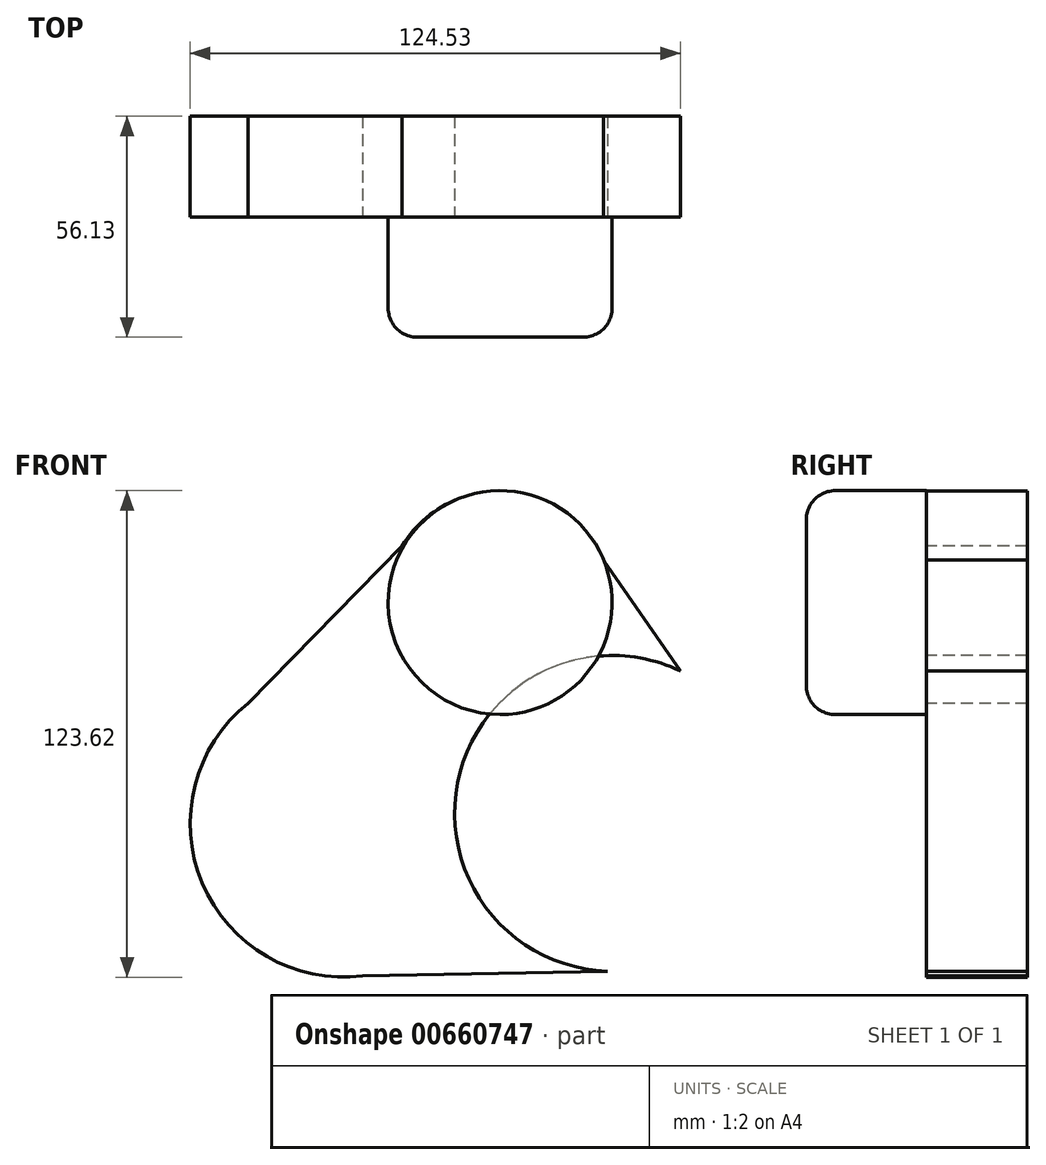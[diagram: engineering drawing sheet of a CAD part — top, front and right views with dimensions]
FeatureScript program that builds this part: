
annotation { "Feature Type Name" : "Feature", "Feature Type Description" : "" }
export const myFeature = defineFeature(function(context is Context, id is Id, definition is map)
    precondition{}
    {
        {
            var Q0;
            Q0=qCreatedBy(makeId("Front.planeOp"),FACE);
            var sketch = newSketch(context, id + "F0", { "sketchPlane" : qUnion([Q0])});
            skCircle(sketch, "E0", {"center": v(-18.53, 30.7) * mm, "radius": 28.78 * mm});
            skCircle(sketch, "E1", {"center": v(-57.98, -24.98) * mm, "radius": 39.05 * mm});
            skCircle(sketch, "E2", {"center": v(10.23, -22.4) * mm, "radius": 40.1 * mm});
            skLineSegment(sketch, "E3", {"start": v(-82.28, 5.58) * mm, "end": v(-43.17, 45.57) * mm});
            skLineSegment(sketch, "E4", {"start": v(7.96, 41.95) * mm, "end": v(27.5, 13.8) * mm});
            skLineSegment(sketch, "E5", {"start": v(-53.18, -63.73) * mm, "end": v(8.94, -62.48) * mm});
            skSolve(sketch);
        }
        {
            var Q0;
            {var subQ0=sQuery(id+"F0.wireOp",EDGE,"E2");var subQ1=sQuery(id+"F0.wireOp",EDGE,"E0");var subQ2=makeQuery(id+"F0.imprint","INTERSECT",VERTEX,{"disambiguationData":[OD(0.0)],"derivedFrom":[subQ1,subQ0]});Q0=makeQuery(id+"F0.imprint","IMPRINT",FACE,{"disambiguationData":[TD([[makeQuery(id+"F0.imprint","IMPRINT",EDGE,{"disambiguationData":[TD([[subQ2,-1.0]])],"derivedFrom":subQ1}),1.0]])]});}
            var Q1;
            {var subQ0=sQuery(id+"F0.wireOp",EDGE,"E4");Q1=makeQuery(id+"F0.imprint","IMPRINT",FACE,{"disambiguationData":[TD([[makeQuery(id+"F0.imprint","IMPRINT",EDGE,{"derivedFrom":subQ0}),-1.0]])]});}
            var Q2;
            {var subQ0=sQuery(id+"F0.wireOp",EDGE,"E5");Q2=makeQuery(id+"F0.imprint","IMPRINT",FACE,{"disambiguationData":[TD([[makeQuery(id+"F0.imprint","IMPRINT",EDGE,{"derivedFrom":subQ0}),1.0]])]});}
            var Q3;
            {var subQ0=sQuery(id+"F0.wireOp",EDGE,"E2");var subQ1=sQuery(id+"F0.wireOp",EDGE,"E1");var subQ2=makeQuery(id+"F0.imprint","INTERSECT",VERTEX,{"disambiguationData":[OD(0.0)],"derivedFrom":[subQ1,subQ0]});Q3=makeQuery(id+"F0.imprint","IMPRINT",FACE,{"disambiguationData":[TD([[makeQuery(id+"F0.imprint","IMPRINT",EDGE,{"disambiguationData":[TD([[subQ2,1.0]])],"derivedFrom":subQ1}),1.0]])]});}
            var Q4;
            {var subQ0=sQuery(id+"F0.wireOp",EDGE,"E2");var subQ1=sQuery(id+"F0.wireOp",EDGE,"E0");var subQ2=makeQuery(id+"F0.imprint","INTERSECT",VERTEX,{"disambiguationData":[OD(0.0)],"derivedFrom":[subQ1,subQ0]});Q4=makeQuery(id+"F0.imprint","IMPRINT",FACE,{"disambiguationData":[TD([[makeQuery(id+"F0.imprint","IMPRINT",EDGE,{"disambiguationData":[TD([[subQ2,-1.0]])],"derivedFrom":subQ1}),-1.0]])]});}
            var Q5;
            {var subQ0=sQuery(id+"F0.wireOp",EDGE,"E0");var subQ1=makeQuery(id+"F0.imprint","INTERSECT",VERTEX,{"derivedFrom":[subQ0,sQuery(id+"F0.wireOp",EDGE,"E3")]});Q5=makeQuery(id+"F0.imprint","IMPRINT",FACE,{"disambiguationData":[TD([[makeQuery(id+"F0.imprint","IMPRINT",EDGE,{"disambiguationData":[TD([[subQ1,1.0]])],"derivedFrom":subQ0}),1.0]])]});}
            var Q6;
            {var subQ0=sQuery(id+"F0.wireOp",EDGE,"E3");Q6=makeQuery(id+"F0.imprint","IMPRINT",FACE,{"disambiguationData":[TD([[makeQuery(id+"F0.imprint","IMPRINT",EDGE,{"derivedFrom":subQ0}),-1.0]])]});}
            var Q7;
            {var subQ0=sQuery(id+"F0.wireOp",EDGE,"E1");var subQ1=makeQuery(id+"F0.imprint","INTERSECT",VERTEX,{"derivedFrom":[subQ0,sQuery(id+"F0.wireOp",EDGE,"E3")]});Q7=makeQuery(id+"F0.imprint","IMPRINT",FACE,{"disambiguationData":[TD([[makeQuery(id+"F0.imprint","IMPRINT",EDGE,{"disambiguationData":[TD([[subQ1,1.0]])],"derivedFrom":subQ0}),1.0]])]});}
            extrude(context, id + "F1", {"entities" : qUnion([Q0, Q1, Q2, Q3, Q4, Q5, Q6, Q7]), "oppositeDirection" : true, "depth" : 25.65 * mm, "offsetDistance" : 25.4 * mm});
        }
        {
            var Q0;
            Q0=qCreatedBy(makeId("Front.planeOp"),FACE);
            var sketch = newSketch(context, id + "F2", { "sketchPlane" : qUnion([Q0])});
            skCircle(sketch, "E6", {"center": v(-18.3, 31.15) * mm, "radius": 28.44 * mm});
            skSolve(sketch);
        }
        {
            var Q0;
            Q0 = qSketchRegion(id + "F2", true);
            extrude(context, id + "F3", {"entities" : qUnion([Q0]), "operationType" : NewBodyOperationType.ADD, "depth" : 30.48 * mm, "offsetDistance" : 25.4 * mm});
        }
        {
            var Q0;
            Q0=makeQuery(id+"F3.opExtrude","CAP_EDGE",EDGE,{"disambiguationData":[OSD([sQuery(id+"F2.wireOp",EDGE,"E6")])],"isStart":false});
            fillet(context, id + "F4", {"entities" : qUnion([Q0]), "radius" : 7.36 * mm, "tangentPropagation" : true, "allowEdgeOverflow" : false});
        }
    });
